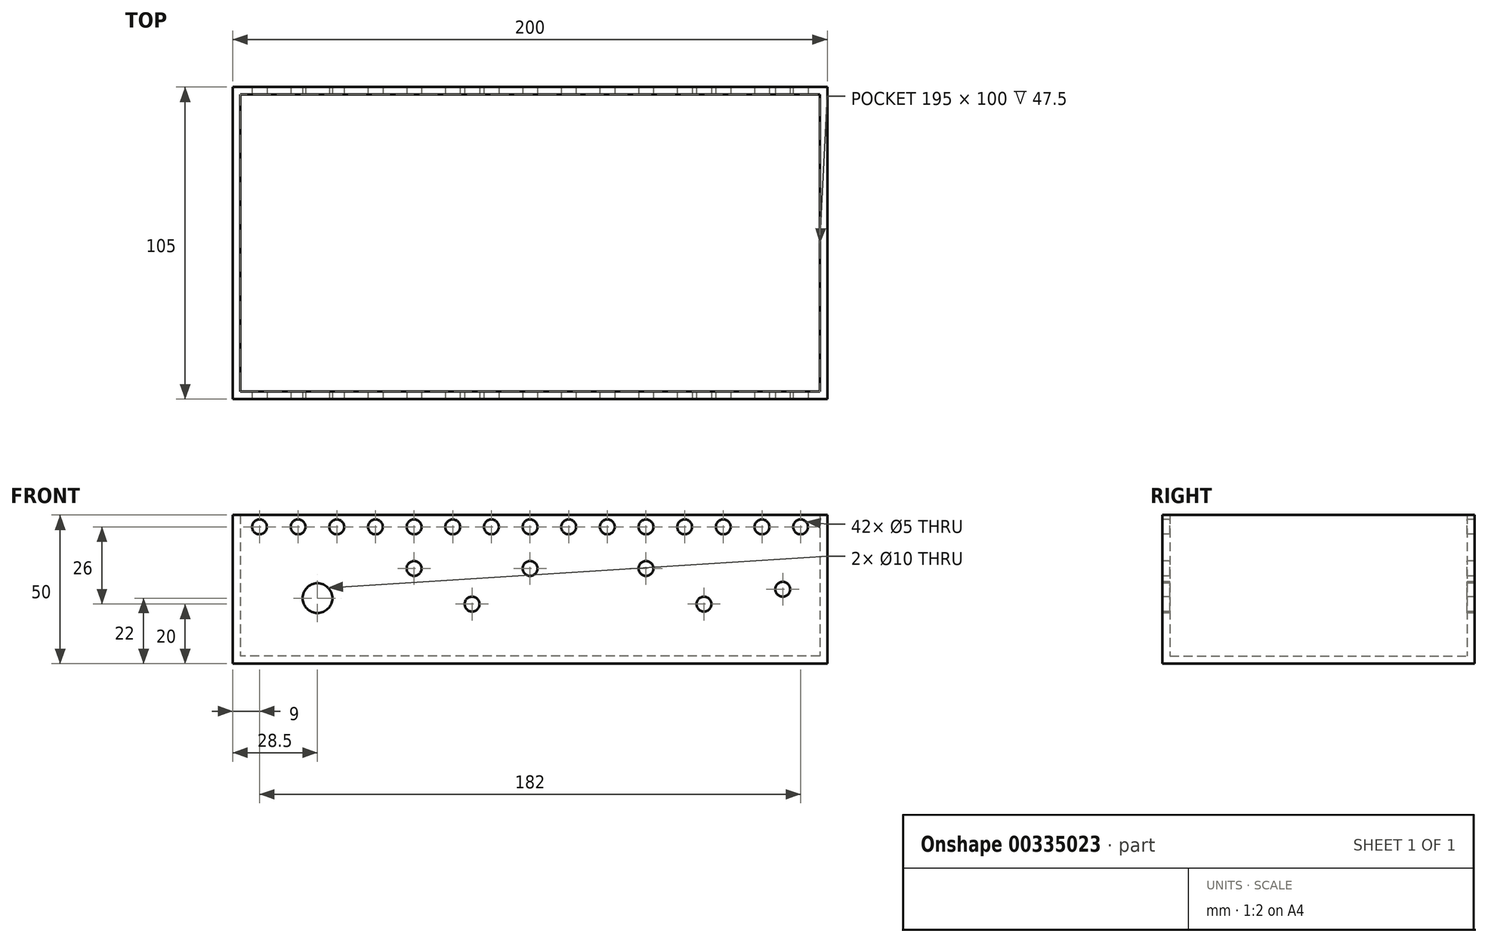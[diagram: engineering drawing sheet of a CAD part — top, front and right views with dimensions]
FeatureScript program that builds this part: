
annotation { "Feature Type Name" : "Feature", "Feature Type Description" : "" }
export const myFeature = defineFeature(function(context is Context, id is Id, definition is map)
    precondition{}
    {
        {
            var Q0;
            Q0=qCreatedBy(makeId("Top.planeOp"),FACE);
            var sketch = newSketch(context, id + "F0", { "sketchPlane" : qUnion([Q0])});
            skLineSegment(sketch, "E0.bottom", {"start": v(100, -52.5) * mm, "end": v(-100, -52.5) * mm});
            skLineSegment(sketch, "E0.top", {"start": v(100, 52.5) * mm, "end": v(-100, 52.5) * mm});
            skLineSegment(sketch, "E0.left", {"start": v(100, -52.5) * mm, "end": v(100, 52.5) * mm});
            skLineSegment(sketch, "E0.right", {"start": v(-100, -52.5) * mm, "end": v(-100, 52.5) * mm});
            skPoint(sketch, "E0.middle", {"position": v(0, 0) * mm});
            skSolve(sketch);
        }
        {
            var Q0;
            Q0=makeQuery(id+"F0.imprint","IMPRINT",FACE,{"disambiguationData":[TD([[makeQuery(id+"F0.imprint","IMPRINT",EDGE,{"derivedFrom":sQuery(id+"F0.wireOp",EDGE,"E0.bottom")}),-1.0]])]});
            extrude(context, id + "F1", {"entities" : qUnion([Q0]), "depth" : 50 * mm});
        }
        {
            var Q0;
            Q0=makeQuery(id+"F1.opExtrude","CAP_FACE",FACE,{"disambiguationData":[OSD([sQuery(id+"F0.wireOp",EDGE,"E0.bottom"),sQuery(id+"F0.wireOp",EDGE,"E0.top"),sQuery(id+"F0.wireOp",EDGE,"E0.left"),sQuery(id+"F0.wireOp",EDGE,"E0.right")])],"isStart":false});
            shell(context, id + "F2", {"entities" : qUnion([Q0]), "thickness" : 2.5 * mm});
        }
        {
            var Q0;
            Q0=makeQuery(id+"F1.opExtrude","SWEPT_FACE",FACE,{"disambiguationData":[OSD([sQuery(id+"F0.wireOp",EDGE,"E0.bottom")])]});
            var sketch = newSketch(context, id + "F3", { "sketchPlane" : qUnion([Q0])});
            skLineSegment(sketch, "E1", {"start": v(0, 50) * mm, "end": v(0, 46) * mm, "construction": true});
            skPoint(sketch, "E1.endSnap0", {"position": v(0, 50) * mm});
            skCircle(sketch, "E2.2.0.0", {"center": v(-91, 46) * mm, "radius": 2.5 * mm});
            skCircle(sketch, "E3.1.0.0", {"center": v(-78, 46) * mm, "radius": 2.5 * mm});
            skCircle(sketch, "E3.2.0.0", {"center": v(-65, 46) * mm, "radius": 2.5 * mm});
            skCircle(sketch, "E3.3.0.0", {"center": v(-52, 46) * mm, "radius": 2.5 * mm});
            skCircle(sketch, "E3.4.0.0", {"center": v(-39, 46) * mm, "radius": 2.5 * mm});
            skCircle(sketch, "E3.5.0.0", {"center": v(-26, 46) * mm, "radius": 2.5 * mm});
            skLineSegment(sketch, "E3.direction1", {"start": v(-91, 46) * mm, "end": v(-78, 46) * mm, "construction": true});
            skCircle(sketch, "E4.0.6.0", {"center": v(-13, 46) * mm, "radius": 2.5 * mm});
            skCircle(sketch, "E4.0.7.0", {"center": v(0, 46) * mm, "radius": 2.5 * mm});
            skCircle(sketch, "E4.0.8.0", {"center": v(13, 46) * mm, "radius": 2.5 * mm});
            skCircle(sketch, "E4.0.9.0", {"center": v(26, 46) * mm, "radius": 2.5 * mm});
            skCircle(sketch, "E4.0.10.0", {"center": v(39, 46) * mm, "radius": 2.5 * mm});
            skCircle(sketch, "E4.0.11.0", {"center": v(52, 46) * mm, "radius": 2.5 * mm});
            skCircle(sketch, "E4.0.12.0", {"center": v(65, 46) * mm, "radius": 2.5 * mm});
            skCircle(sketch, "E4.0.13.0", {"center": v(78, 46) * mm, "radius": 2.5 * mm});
            skCircle(sketch, "E4.0.14.0", {"center": v(91, 46) * mm, "radius": 2.5 * mm});
            skLineSegment(sketch, "E5", {"start": v(0, 0) * mm, "end": v(0, 32) * mm, "construction": true});
            skLineSegment(sketch, "E6", {"start": v(0, 32) * mm, "end": v(100, 32) * mm, "construction": true});
            skLineSegment(sketch, "E7", {"start": v(0, 32) * mm, "end": v(-100, 32) * mm, "construction": true});
            skCircle(sketch, "E8.1.0.0", {"center": v(-39, 32) * mm, "radius": 2.5 * mm});
            skCircle(sketch, "E8.2.0.0", {"center": v(0, 32) * mm, "radius": 2.5 * mm});
            skCircle(sketch, "E8.3.0.0", {"center": v(39, 32) * mm, "radius": 2.5 * mm});
            skLineSegment(sketch, "E8.direction1", {"start": v(-78, 32) * mm, "end": v(-39, 32) * mm, "construction": true});
            skLineSegment(sketch, "E9", {"start": v(-100, 22) * mm, "end": v(100, 22) * mm, "construction": true});
            skCircle(sketch, "E10", {"center": v(-71.5, 22) * mm, "radius": 5 * mm});
            skCircle(sketch, "E11", {"center": v(-19.5, 20) * mm, "radius": 2.5 * mm});
            skCircle(sketch, "E12", {"center": v(58.5, 20) * mm, "radius": 2.5 * mm});
            skCircle(sketch, "E13", {"center": v(85, 25) * mm, "radius": 2.5 * mm});
            skSolve(sketch);
        }
        {
            var Q0;
            Q0 = qSketchRegion(id + "F3", true);
            var Q1;
            Q1=makeQuery(id+"F1.opExtrude","SWEPT_FACE",FACE,{"disambiguationData":[OSD([sQuery(id+"F0.wireOp",EDGE,"E0.top")])]});
            extrude(context, id + "F4", {"entities" : qUnion([Q0]), "operationType" : NewBodyOperationType.REMOVE, "endBound" : BoundingType.UP_TO_SURFACE, "oppositeDirection" : true, "endBoundEntityFace" : qUnion([Q1]), "depth" : 138.9 * mm});
        }
    });
